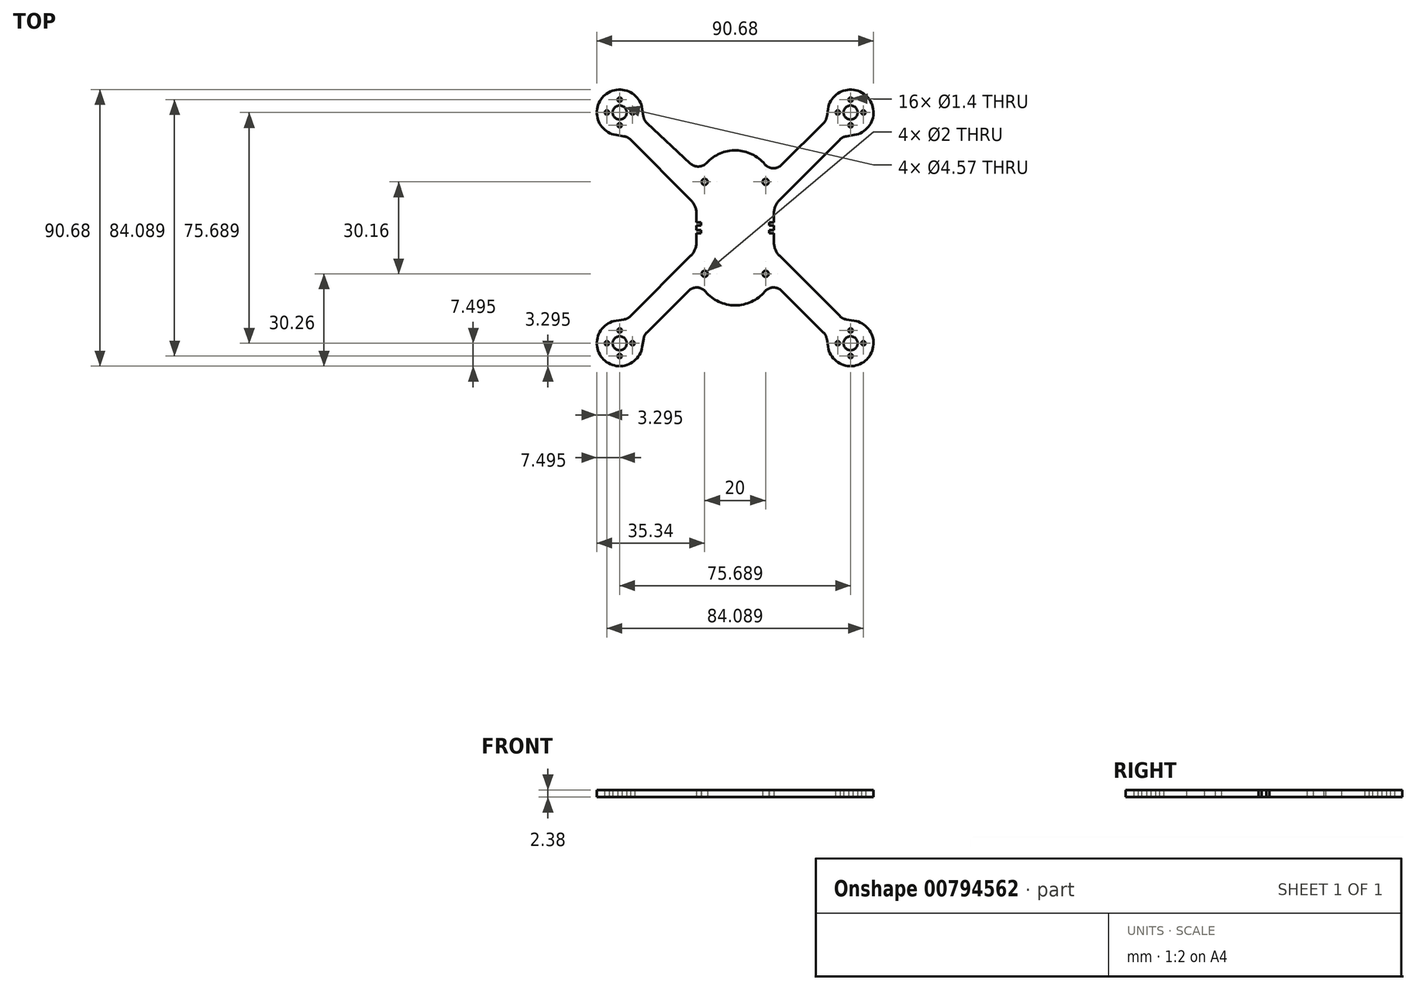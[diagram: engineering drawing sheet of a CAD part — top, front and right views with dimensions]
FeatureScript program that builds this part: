
annotation { "Feature Type Name" : "Feature", "Feature Type Description" : "" }
export const myFeature = defineFeature(function(context is Context, id is Id, definition is map)
    precondition{}
    {
        {
            var Q0;
            Q0=qCreatedBy(makeId("Top.planeOp"),FACE);
            var sketch = newSketch(context, id + "F0", { "sketchPlane" : qUnion([Q0])});
            skLineSegment(sketch, "E0.bottom", {"start": v(0, -25.4) * mm, "end": v(0, -25.4) * mm});
            skLineSegment(sketch, "E0.top", {"start": v(0, 25.4) * mm, "end": v(0, 25.4) * mm});
            skLineSegment(sketch, "E0.left", {"start": v(12.7, -4.68) * mm, "end": v(12.7, 4.68) * mm});
            skLineSegment(sketch, "E0.right", {"start": v(-12.7, -4.68) * mm, "end": v(-12.7, 4.68) * mm});
            skPoint(sketch, "E0.middle", {"position": v(0, 0) * mm});
            skLineSegment(sketch, "E1", {"start": v(12.7, 12.7) * mm, "end": v(37.84, 37.84) * mm});
            skLineSegment(sketch, "E2", {"start": v(-12.7, 12.7) * mm, "end": v(-37.84, 37.84) * mm});
            skLineSegment(sketch, "E3", {"start": v(-12.7, -12.7) * mm, "end": v(-37.84, -37.84) * mm});
            skLineSegment(sketch, "E4", {"start": v(12.7, -12.7) * mm, "end": v(37.84, -37.84) * mm});
            skPoint(sketch, "E5.visualSharp", {"position": v(12.7, -25.4) * mm});
            skArc(sketch, "E5.filletArc", {"start": v(0, -25.4) * mm, "mid": v(5.34, -24.22) * mm, "end": v(9.69, -20.9) * mm});
            skPoint(sketch, "E6.visualSharp", {"position": v(-12.7, -25.4) * mm});
            skArc(sketch, "E6.filletArc", {"start": v(-9.69, -20.9) * mm, "mid": v(-5.34, -24.22) * mm, "end": v(0, -25.4) * mm});
            skPoint(sketch, "E7.visualSharp", {"position": v(-12.7, 25.4) * mm});
            skArc(sketch, "E7.filletArc", {"start": v(0, 25.4) * mm, "mid": v(-5.07, 24.34) * mm, "end": v(-9.3, 21.35) * mm});
            skPoint(sketch, "E8.visualSharp", {"position": v(12.7, 25.4) * mm});
            skArc(sketch, "E8.filletArc", {"start": v(9.69, 20.9) * mm, "mid": v(5.34, 24.22) * mm, "end": v(0, 25.4) * mm});
            skLineSegment(sketch, "E9.bottom", {"start": v(10, -10) * mm, "end": v(-10, -10) * mm});
            skLineSegment(sketch, "E9.top", {"start": v(10, 10) * mm, "end": v(-10, 10) * mm});
            skLineSegment(sketch, "E9.left", {"start": v(10, -10) * mm, "end": v(10, 10) * mm});
            skLineSegment(sketch, "E9.right", {"start": v(-10, -10) * mm, "end": v(-10, 10) * mm});
            skCircle(sketch, "E10", {"center": v(37.84, -37.84) * mm, "radius": 7.5 * mm});
            skCircle(sketch, "E11", {"center": v(-37.84, -37.84) * mm, "radius": 7.5 * mm});
            skCircle(sketch, "E12", {"center": v(-37.84, 37.84) * mm, "radius": 7.5 * mm});
            skCircle(sketch, "E13", {"center": v(37.84, 37.84) * mm, "radius": 7.5 * mm});
            skLineSegment(sketch, "E14", {"start": v(-32.54, -32.54) * mm, "end": v(-35.24, -29.85) * mm});
            skLineSegment(sketch, "E15", {"start": v(-32.54, -32.54) * mm, "end": v(-29.85, -35.24) * mm});
            skLineSegment(sketch, "E16", {"start": v(-36.46, -30.04) * mm, "end": v(-39, -30.43) * mm});
            skLineSegment(sketch, "E17", {"start": v(-30.04, -36.46) * mm, "end": v(-30.43, -39) * mm});
            skLineSegment(sketch, "E18", {"start": v(-32.54, 32.54) * mm, "end": v(-35.24, 29.85) * mm});
            skLineSegment(sketch, "E19", {"start": v(-32.54, 32.54) * mm, "end": v(-29.85, 35.24) * mm});
            skLineSegment(sketch, "E20", {"start": v(-30.05, 36.54) * mm, "end": v(-30.43, 39) * mm});
            skLineSegment(sketch, "E21", {"start": v(-36.46, 30.04) * mm, "end": v(-39, 30.43) * mm});
            skLineSegment(sketch, "E22", {"start": v(32.54, 32.54) * mm, "end": v(35.24, 29.85) * mm});
            skLineSegment(sketch, "E23", {"start": v(32.54, 32.54) * mm, "end": v(29.85, 35.24) * mm});
            skLineSegment(sketch, "E24", {"start": v(36.46, 30.04) * mm, "end": v(39, 30.43) * mm});
            skLineSegment(sketch, "E25", {"start": v(30.04, 36.46) * mm, "end": v(30.43, 39) * mm});
            skLineSegment(sketch, "E26", {"start": v(-34.36, -28.97) * mm, "end": v(-14.56, -9.17) * mm});
            skLineSegment(sketch, "E27", {"start": v(-28.97, -34.36) * mm, "end": v(-15.3, -20.68) * mm});
            skLineSegment(sketch, "E28", {"start": v(-28.88, 34.34) * mm, "end": v(-14.68, 21.15) * mm});
            skLineSegment(sketch, "E29", {"start": v(-34.36, 28.97) * mm, "end": v(-14.56, 9.17) * mm});
            skLineSegment(sketch, "E30", {"start": v(34.36, 28.97) * mm, "end": v(14.56, 9.17) * mm});
            skLineSegment(sketch, "E31", {"start": v(28.97, 34.36) * mm, "end": v(15.3, 20.68) * mm});
            skLineSegment(sketch, "E32", {"start": v(32.54, -32.54) * mm, "end": v(35.24, -29.85) * mm});
            skLineSegment(sketch, "E33", {"start": v(32.54, -32.54) * mm, "end": v(29.85, -35.24) * mm});
            skLineSegment(sketch, "E34", {"start": v(36.46, -30.04) * mm, "end": v(39, -30.43) * mm});
            skLineSegment(sketch, "E35", {"start": v(30.04, -36.46) * mm, "end": v(30.43, -39) * mm});
            skLineSegment(sketch, "E36", {"start": v(28.97, -34.36) * mm, "end": v(15.3, -20.68) * mm});
            skLineSegment(sketch, "E37", {"start": v(34.36, -28.97) * mm, "end": v(14.56, -9.17) * mm});
            skArc(sketch, "E38.filletArc", {"start": v(-12.7, 4.68) * mm, "mid": v(-13.18, 7.11) * mm, "end": v(-14.56, 9.17) * mm});
            skArc(sketch, "E39.filletArc", {"start": v(14.56, 9.17) * mm, "mid": v(13.18, 7.11) * mm, "end": v(12.7, 4.68) * mm});
            skArc(sketch, "E40.filletArc", {"start": v(12.7, -4.68) * mm, "mid": v(13.18, -7.11) * mm, "end": v(14.56, -9.17) * mm});
            skArc(sketch, "E41.filletArc", {"start": v(-14.56, -9.17) * mm, "mid": v(-13.18, -7.11) * mm, "end": v(-12.7, -4.68) * mm});
            skArc(sketch, "E42.filletArc", {"start": v(-14.68, 21.15) * mm, "mid": v(-11.95, 20.14) * mm, "end": v(-9.3, 21.35) * mm});
            skArc(sketch, "E43.filletArc", {"start": v(9.69, 20.9) * mm, "mid": v(12.44, 19.57) * mm, "end": v(15.3, 20.68) * mm});
            skArc(sketch, "E44.filletArc", {"start": v(15.3, -20.68) * mm, "mid": v(12.44, -19.57) * mm, "end": v(9.69, -20.9) * mm});
            skArc(sketch, "E45.filletArc", {"start": v(-9.69, -20.9) * mm, "mid": v(-12.44, -19.57) * mm, "end": v(-15.3, -20.68) * mm});
            skPoint(sketch, "E46.visualSharp", {"position": v(35.24, -29.85) * mm});
            skArc(sketch, "E46.filletArc", {"start": v(34.36, -28.97) * mm, "mid": v(35.33, -29.67) * mm, "end": v(36.46, -30.04) * mm});
            skPoint(sketch, "E47.visualSharp", {"position": v(29.85, -35.24) * mm});
            skArc(sketch, "E47.filletArc", {"start": v(30.04, -36.46) * mm, "mid": v(29.67, -35.33) * mm, "end": v(28.97, -34.36) * mm});
            skPoint(sketch, "E48.visualSharp", {"position": v(-29.85, -35.24) * mm});
            skArc(sketch, "E48.filletArc", {"start": v(-28.97, -34.36) * mm, "mid": v(-29.67, -35.33) * mm, "end": v(-30.04, -36.46) * mm});
            skPoint(sketch, "E49.visualSharp", {"position": v(-35.24, -29.85) * mm});
            skArc(sketch, "E49.filletArc", {"start": v(-36.46, -30.04) * mm, "mid": v(-35.33, -29.67) * mm, "end": v(-34.36, -28.97) * mm});
            skPoint(sketch, "E50.visualSharp", {"position": v(-35.24, 29.85) * mm});
            skArc(sketch, "E50.filletArc", {"start": v(-34.36, 28.97) * mm, "mid": v(-35.33, 29.67) * mm, "end": v(-36.46, 30.04) * mm});
            skPoint(sketch, "E51.visualSharp", {"position": v(-29.85, 35.24) * mm});
            skArc(sketch, "E51.filletArc", {"start": v(-30.05, 36.54) * mm, "mid": v(-29.65, 35.34) * mm, "end": v(-28.88, 34.34) * mm});
            skPoint(sketch, "E52.visualSharp", {"position": v(35.24, 29.85) * mm});
            skArc(sketch, "E52.filletArc", {"start": v(36.46, 30.04) * mm, "mid": v(35.33, 29.67) * mm, "end": v(34.36, 28.97) * mm});
            skPoint(sketch, "E53.visualSharp", {"position": v(29.85, 35.24) * mm});
            skArc(sketch, "E53.filletArc", {"start": v(28.97, 34.36) * mm, "mid": v(29.67, 35.33) * mm, "end": v(30.04, 36.46) * mm});
            skLineSegment(sketch, "E54", {"start": v(12.7, 0) * mm, "end": v(12.7, 0.76) * mm});
            skLineSegment(sketch, "E55", {"start": v(12.7, 0) * mm, "end": v(12.7, -0.76) * mm});
            skLineSegment(sketch, "E56.bottom", {"start": v(12.7, 0.76) * mm, "end": v(11.18, 0.76) * mm});
            skLineSegment(sketch, "E56.top", {"start": v(12.7, 1.78) * mm, "end": v(11.18, 1.78) * mm});
            skLineSegment(sketch, "E56.left", {"start": v(12.7, 0.76) * mm, "end": v(12.7, 1.78) * mm});
            skLineSegment(sketch, "E56.right", {"start": v(11.18, 0.76) * mm, "end": v(11.18, 1.78) * mm});
            skLineSegment(sketch, "E57.bottom", {"start": v(12.7, -0.76) * mm, "end": v(11.18, -0.76) * mm});
            skLineSegment(sketch, "E57.top", {"start": v(12.7, -1.78) * mm, "end": v(11.18, -1.78) * mm});
            skLineSegment(sketch, "E57.left", {"start": v(12.7, -0.76) * mm, "end": v(12.7, -1.78) * mm});
            skLineSegment(sketch, "E57.right", {"start": v(11.18, -0.76) * mm, "end": v(11.18, -1.78) * mm});
            skLineSegment(sketch, "E58", {"start": v(-12.7, 0) * mm, "end": v(-12.7, 0.76) * mm});
            skLineSegment(sketch, "E59", {"start": v(-12.7, 0) * mm, "end": v(-12.7, -0.76) * mm});
            skLineSegment(sketch, "E60.bottom", {"start": v(-12.7, 0.76) * mm, "end": v(-11.18, 0.76) * mm});
            skLineSegment(sketch, "E60.top", {"start": v(-12.7, 1.78) * mm, "end": v(-11.18, 1.78) * mm});
            skLineSegment(sketch, "E60.left", {"start": v(-12.7, 0.76) * mm, "end": v(-12.7, 1.78) * mm});
            skLineSegment(sketch, "E60.right", {"start": v(-11.18, 0.76) * mm, "end": v(-11.18, 1.78) * mm});
            skLineSegment(sketch, "E61.bottom", {"start": v(-12.7, -0.76) * mm, "end": v(-11.18, -0.76) * mm});
            skLineSegment(sketch, "E61.top", {"start": v(-12.7, -1.78) * mm, "end": v(-11.18, -1.78) * mm});
            skLineSegment(sketch, "E61.left", {"start": v(-12.7, -0.76) * mm, "end": v(-12.7, -1.78) * mm});
            skLineSegment(sketch, "E61.right", {"start": v(-11.18, -0.76) * mm, "end": v(-11.18, -1.78) * mm});
            skCircle(sketch, "E62", {"center": v(-37.84, 37.84) * mm, "radius": 4.2 * mm});
            skLineSegment(sketch, "E63", {"start": v(-37.84, 37.84) * mm, "end": v(-33.64, 37.84) * mm});
            skLineSegment(sketch, "E64", {"start": v(-37.84, 37.84) * mm, "end": v(-37.84, 33.64) * mm});
            skLineSegment(sketch, "E65", {"start": v(-37.84, 37.84) * mm, "end": v(-37.84, 42.04) * mm});
            skLineSegment(sketch, "E66", {"start": v(-37.84, 37.84) * mm, "end": v(-42.04, 37.84) * mm});
            skCircle(sketch, "E67", {"center": v(-37.84, 42.04) * mm, "radius": 0.7 * mm});
            skCircle(sketch, "E68", {"center": v(-33.64, 37.84) * mm, "radius": 0.7 * mm});
            skCircle(sketch, "E69", {"center": v(-37.84, 33.64) * mm, "radius": 0.7 * mm});
            skCircle(sketch, "E70", {"center": v(-42.04, 37.84) * mm, "radius": 0.7 * mm});
            skCircle(sketch, "E71", {"center": v(37.84, 37.84) * mm, "radius": 4.2 * mm});
            skLineSegment(sketch, "E72", {"start": v(37.84, 37.84) * mm, "end": v(33.64, 37.84) * mm});
            skLineSegment(sketch, "E73", {"start": v(37.84, 37.84) * mm, "end": v(37.84, 33.64) * mm});
            skLineSegment(sketch, "E74", {"start": v(37.84, 37.84) * mm, "end": v(42.04, 37.84) * mm});
            skLineSegment(sketch, "E75", {"start": v(37.84, 37.84) * mm, "end": v(37.84, 42.04) * mm});
            skCircle(sketch, "E76", {"center": v(33.64, 37.84) * mm, "radius": 0.7 * mm});
            skCircle(sketch, "E77", {"center": v(37.84, 42.04) * mm, "radius": 0.7 * mm});
            skCircle(sketch, "E78", {"center": v(42.04, 37.84) * mm, "radius": 0.7 * mm});
            skCircle(sketch, "E79", {"center": v(37.84, 33.64) * mm, "radius": 0.7 * mm});
            skCircle(sketch, "E80", {"center": v(37.84, -37.84) * mm, "radius": 4.2 * mm});
            skLineSegment(sketch, "E81", {"start": v(37.84, -37.84) * mm, "end": v(37.84, -33.64) * mm});
            skLineSegment(sketch, "E82", {"start": v(37.84, -37.84) * mm, "end": v(33.64, -37.84) * mm});
            skLineSegment(sketch, "E83", {"start": v(37.84, -37.84) * mm, "end": v(42.04, -37.84) * mm});
            skLineSegment(sketch, "E84", {"start": v(37.84, -37.84) * mm, "end": v(37.84, -42.04) * mm});
            skCircle(sketch, "E85", {"center": v(33.64, -37.84) * mm, "radius": 0.7 * mm});
            skCircle(sketch, "E86", {"center": v(37.84, -33.64) * mm, "radius": 0.7 * mm});
            skCircle(sketch, "E87", {"center": v(42.04, -37.84) * mm, "radius": 0.7 * mm});
            skCircle(sketch, "E88", {"center": v(37.84, -42.04) * mm, "radius": 0.7 * mm});
            skCircle(sketch, "E89", {"center": v(-37.84, -37.84) * mm, "radius": 4.2 * mm});
            skLineSegment(sketch, "E90", {"start": v(-37.84, -37.84) * mm, "end": v(-33.64, -37.84) * mm});
            skLineSegment(sketch, "E91", {"start": v(-37.84, -37.84) * mm, "end": v(-37.84, -33.64) * mm});
            skLineSegment(sketch, "E92", {"start": v(-37.84, -37.84) * mm, "end": v(-37.84, -42.04) * mm});
            skLineSegment(sketch, "E93", {"start": v(-37.84, -37.84) * mm, "end": v(-42.04, -37.84) * mm});
            skCircle(sketch, "E94", {"center": v(-42.04, -37.84) * mm, "radius": 0.7 * mm});
            skCircle(sketch, "E95", {"center": v(-37.84, -33.64) * mm, "radius": 0.7 * mm});
            skCircle(sketch, "E96", {"center": v(-33.64, -37.84) * mm, "radius": 0.7 * mm});
            skCircle(sketch, "E97", {"center": v(-37.84, -42.04) * mm, "radius": 0.7 * mm});
            skCircle(sketch, "E98", {"center": v(37.84, 37.84) * mm, "radius": 2.29 * mm});
            skCircle(sketch, "E99", {"center": v(-37.84, 37.84) * mm, "radius": 2.29 * mm});
            skCircle(sketch, "E100", {"center": v(-37.84, -37.84) * mm, "radius": 2.29 * mm});
            skCircle(sketch, "E101", {"center": v(37.84, -37.84) * mm, "radius": 2.29 * mm});
            skLineSegment(sketch, "E102", {"start": v(-10, 10) * mm, "end": v(-10, 15.08) * mm});
            skLineSegment(sketch, "E103", {"start": v(-10, -10) * mm, "end": v(-10, -15.08) * mm});
            skLineSegment(sketch, "E104", {"start": v(10, -10) * mm, "end": v(10, -15.08) * mm});
            skLineSegment(sketch, "E105", {"start": v(10, 10) * mm, "end": v(10, 15.08) * mm});
            skCircle(sketch, "E106", {"center": v(-10, 15.08) * mm, "radius": 1 * mm});
            skCircle(sketch, "E107", {"center": v(10, 15.08) * mm, "radius": 1 * mm});
            skCircle(sketch, "E108", {"center": v(-10, -15.08) * mm, "radius": 1 * mm});
            skCircle(sketch, "E109", {"center": v(10, -15.08) * mm, "radius": 1 * mm});
            skSolve(sketch);
        }
        {
            var Q0;
            {var subQ5=sQuery(id+"F0.wireOp",EDGE,"E85");var subQ6=sQuery(id+"F0.wireOp",EDGE,"E80");var subQ7=makeQuery(id+"F0.imprint","INTERSECT",VERTEX,{"disambiguationData":[OD(1.0)],"derivedFrom":[subQ6,subQ5]});Q0=makeQuery(id+"F0.imprint","IMPRINT",FACE,{"disambiguationData":[TD([[makeQuery(id+"F0.imprint","IMPRINT",EDGE,{"disambiguationData":[TD([[subQ7,-1.0]])],"derivedFrom":subQ6}),1.0]])]});}
            var Q1;
            {var subQ1=sQuery(id+"F0.wireOp",EDGE,"E71");var subQ7=sQuery(id+"F0.wireOp",EDGE,"E77");var subQ8=makeQuery(id+"F0.imprint","INTERSECT",VERTEX,{"disambiguationData":[OD(1.0)],"derivedFrom":[subQ1,subQ7]});Q1=makeQuery(id+"F0.imprint","IMPRINT",FACE,{"disambiguationData":[TD([[makeQuery(id+"F0.imprint","IMPRINT",EDGE,{"disambiguationData":[TD([[subQ8,-1.0]])],"derivedFrom":subQ1}),1.0]])]});}
            var Q2;
            {var subQ1=sQuery(id+"F0.wireOp",EDGE,"E71");var subQ7=sQuery(id+"F0.wireOp",EDGE,"E78");var subQ9=makeQuery(id+"F0.imprint","INTERSECT",VERTEX,{"disambiguationData":[OD(0.0)],"derivedFrom":[subQ1,subQ7]});Q2=makeQuery(id+"F0.imprint","IMPRINT",FACE,{"disambiguationData":[TD([[makeQuery(id+"F0.imprint","IMPRINT",EDGE,{"disambiguationData":[TD([[subQ9,-1.0]])],"derivedFrom":subQ1}),1.0]])]});}
            var Q3;
            {var subQ1=sQuery(id+"F0.wireOp",EDGE,"E1");var subQ3=sQuery(id+"F0.wireOp",EDGE,"E71");var subQ4=makeQuery(id+"F0.imprint","INTERSECT",VERTEX,{"derivedFrom":[subQ1,subQ3]});Q3=makeQuery(id+"F0.imprint","IMPRINT",FACE,{"disambiguationData":[TD([[makeQuery(id+"F0.imprint","IMPRINT",EDGE,{"disambiguationData":[TD([[subQ4,-1.0]])],"derivedFrom":subQ3}),1.0]])]});}
            var Q4;
            {var subQ1=sQuery(id+"F0.wireOp",EDGE,"E89");var subQ7=sQuery(id+"F0.wireOp",EDGE,"E95");var subQ9=makeQuery(id+"F0.imprint","INTERSECT",VERTEX,{"disambiguationData":[OD(1.0)],"derivedFrom":[subQ1,subQ7]});Q4=makeQuery(id+"F0.imprint","IMPRINT",FACE,{"disambiguationData":[TD([[makeQuery(id+"F0.imprint","IMPRINT",EDGE,{"disambiguationData":[TD([[subQ9,-1.0]])],"derivedFrom":subQ1}),1.0]])]});}
            var Q5;
            Q5=makeQuery(id+"F0.imprint","IMPRINT",FACE,{"disambiguationData":[TD([[makeQuery(id+"F0.imprint","IMPRINT",EDGE,{"derivedFrom":sQuery(id+"F0.wireOp",EDGE,"E9.bottom")}),-1.0]])]});
            var Q6;
            {var subQ1=sQuery(id+"F0.wireOp",EDGE,"E80");var subQ7=sQuery(id+"F0.wireOp",EDGE,"E87");var subQ9=makeQuery(id+"F0.imprint","INTERSECT",VERTEX,{"disambiguationData":[OD(0.0)],"derivedFrom":[subQ1,subQ7]});Q6=makeQuery(id+"F0.imprint","IMPRINT",FACE,{"disambiguationData":[TD([[makeQuery(id+"F0.imprint","IMPRINT",EDGE,{"disambiguationData":[TD([[subQ9,-1.0]])],"derivedFrom":subQ1}),1.0]])]});}
            var Q7;
            {var subQ4=sQuery(id+"F0.wireOp",EDGE,"E12");var subQ15=makeQuery(id+"F0.imprint","IMPRINT",VERTEX,{"derivedFrom":subQ4});Q7=makeQuery(id+"F0.imprint","IMPRINT",FACE,{"disambiguationData":[TD([[makeQuery(id+"F0.imprint","IMPRINT",EDGE,{"disambiguationData":[TD([[subQ15,1.0]])],"derivedFrom":subQ4}),1.0]])]});}
            var Q8;
            {var subQ1=sQuery(id+"F0.wireOp",EDGE,"E4");var subQ3=sQuery(id+"F0.wireOp",EDGE,"E80");var subQ4=makeQuery(id+"F0.imprint","INTERSECT",VERTEX,{"derivedFrom":[subQ1,subQ3]});Q8=makeQuery(id+"F0.imprint","IMPRINT",FACE,{"disambiguationData":[TD([[makeQuery(id+"F0.imprint","IMPRINT",EDGE,{"disambiguationData":[TD([[subQ4,-1.0]])],"derivedFrom":subQ3}),1.0]])]});}
            var Q9;
            {var subQ1=sQuery(id+"F0.wireOp",EDGE,"E71");var subQ7=sQuery(id+"F0.wireOp",EDGE,"E79");var subQ9=makeQuery(id+"F0.imprint","INTERSECT",VERTEX,{"disambiguationData":[OD(1.0)],"derivedFrom":[subQ1,subQ7]});Q9=makeQuery(id+"F0.imprint","IMPRINT",FACE,{"disambiguationData":[TD([[makeQuery(id+"F0.imprint","IMPRINT",EDGE,{"disambiguationData":[TD([[subQ9,-1.0]])],"derivedFrom":subQ1}),1.0]])]});}
            var Q10;
            {var subQ1=sQuery(id+"F0.wireOp",EDGE,"E2");var subQ3=sQuery(id+"F0.wireOp",EDGE,"E62");var subQ4=makeQuery(id+"F0.imprint","INTERSECT",VERTEX,{"derivedFrom":[subQ1,subQ3]});Q10=makeQuery(id+"F0.imprint","IMPRINT",FACE,{"disambiguationData":[TD([[makeQuery(id+"F0.imprint","IMPRINT",EDGE,{"disambiguationData":[TD([[subQ4,1.0]])],"derivedFrom":subQ3}),1.0]])]});}
            var Q11;
            {var subQ0=sQuery(id+"F0.wireOp",EDGE,"E67");var subQ1=sQuery(id+"F0.wireOp",EDGE,"E62");var subQ2=makeQuery(id+"F0.imprint","INTERSECT",VERTEX,{"disambiguationData":[OD(1.0)],"derivedFrom":[subQ1,subQ0]});Q11=makeQuery(id+"F0.imprint","IMPRINT",FACE,{"disambiguationData":[TD([[makeQuery(id+"F0.imprint","IMPRINT",EDGE,{"disambiguationData":[TD([[subQ2,-1.0]])],"derivedFrom":subQ1}),1.0]])]});}
            var Q12;
            {var subQ4=sQuery(id+"F0.wireOp",EDGE,"E11");var subQ5=makeQuery(id+"F0.imprint","IMPRINT",VERTEX,{"derivedFrom":subQ4});Q12=makeQuery(id+"F0.imprint","IMPRINT",FACE,{"disambiguationData":[TD([[makeQuery(id+"F0.imprint","IMPRINT",EDGE,{"disambiguationData":[TD([[subQ5,-1.0]])],"derivedFrom":subQ4}),1.0]])]});}
            var Q13;
            {var subQ1=sQuery(id+"F0.wireOp",EDGE,"E4");var subQ3=sQuery(id+"F0.wireOp",EDGE,"E80");var subQ4=makeQuery(id+"F0.imprint","INTERSECT",VERTEX,{"derivedFrom":[subQ1,subQ3]});Q13=makeQuery(id+"F0.imprint","IMPRINT",FACE,{"disambiguationData":[TD([[makeQuery(id+"F0.imprint","IMPRINT",EDGE,{"disambiguationData":[TD([[subQ4,1.0]])],"derivedFrom":subQ3}),1.0]])]});}
            var Q14;
            {var subQ1=sQuery(id+"F0.wireOp",EDGE,"E80");var subQ7=sQuery(id+"F0.wireOp",EDGE,"E88");var subQ9=makeQuery(id+"F0.imprint","INTERSECT",VERTEX,{"disambiguationData":[OD(1.0)],"derivedFrom":[subQ1,subQ7]});Q14=makeQuery(id+"F0.imprint","IMPRINT",FACE,{"disambiguationData":[TD([[makeQuery(id+"F0.imprint","IMPRINT",EDGE,{"disambiguationData":[TD([[subQ9,-1.0]])],"derivedFrom":subQ1}),1.0]])]});}
            var Q15;
            {var subQ3=sQuery(id+"F0.wireOp",EDGE,"E94");var subQ5=sQuery(id+"F0.wireOp",EDGE,"E89");var subQ6=makeQuery(id+"F0.imprint","INTERSECT",VERTEX,{"disambiguationData":[OD(1.0)],"derivedFrom":[subQ5,subQ3]});Q15=makeQuery(id+"F0.imprint","IMPRINT",FACE,{"disambiguationData":[TD([[makeQuery(id+"F0.imprint","IMPRINT",EDGE,{"disambiguationData":[TD([[subQ6,-1.0]])],"derivedFrom":subQ5}),1.0]])]});}
            var Q16;
            {var subQ1=sQuery(id+"F0.wireOp",EDGE,"E1");var subQ3=sQuery(id+"F0.wireOp",EDGE,"E71");var subQ4=makeQuery(id+"F0.imprint","INTERSECT",VERTEX,{"derivedFrom":[subQ1,subQ3]});Q16=makeQuery(id+"F0.imprint","IMPRINT",FACE,{"disambiguationData":[TD([[makeQuery(id+"F0.imprint","IMPRINT",EDGE,{"disambiguationData":[TD([[subQ4,1.0]])],"derivedFrom":subQ3}),1.0]])]});}
            var Q17;
            {var subQ1=sQuery(id+"F0.wireOp",EDGE,"E2");var subQ3=sQuery(id+"F0.wireOp",EDGE,"E62");var subQ4=makeQuery(id+"F0.imprint","INTERSECT",VERTEX,{"derivedFrom":[subQ1,subQ3]});Q17=makeQuery(id+"F0.imprint","IMPRINT",FACE,{"disambiguationData":[TD([[makeQuery(id+"F0.imprint","IMPRINT",EDGE,{"disambiguationData":[TD([[subQ4,-1.0]])],"derivedFrom":subQ3}),1.0]])]});}
            var Q18;
            {var subQ3=sQuery(id+"F0.wireOp",EDGE,"E97");var subQ6=sQuery(id+"F0.wireOp",EDGE,"E89");var subQ9=makeQuery(id+"F0.imprint","INTERSECT",VERTEX,{"disambiguationData":[OD(1.0)],"derivedFrom":[subQ6,subQ3]});Q18=makeQuery(id+"F0.imprint","IMPRINT",FACE,{"disambiguationData":[TD([[makeQuery(id+"F0.imprint","IMPRINT",EDGE,{"disambiguationData":[TD([[subQ9,-1.0]])],"derivedFrom":subQ6}),1.0]])]});}
            var Q19;
            {var subQ1=sQuery(id+"F0.wireOp",EDGE,"E62");var subQ7=sQuery(id+"F0.wireOp",EDGE,"E68");var subQ9=makeQuery(id+"F0.imprint","INTERSECT",VERTEX,{"disambiguationData":[OD(0.0)],"derivedFrom":[subQ1,subQ7]});Q19=makeQuery(id+"F0.imprint","IMPRINT",FACE,{"disambiguationData":[TD([[makeQuery(id+"F0.imprint","IMPRINT",EDGE,{"disambiguationData":[TD([[subQ9,-1.0]])],"derivedFrom":subQ1}),1.0]])]});}
            var Q20;
            {var subQ10=sQuery(id+"F0.wireOp",EDGE,"E13");var subQ11=makeQuery(id+"F0.imprint","IMPRINT",VERTEX,{"derivedFrom":subQ10});Q20=makeQuery(id+"F0.imprint","IMPRINT",FACE,{"disambiguationData":[TD([[makeQuery(id+"F0.imprint","IMPRINT",EDGE,{"disambiguationData":[TD([[subQ11,1.0]])],"derivedFrom":subQ10}),1.0]])]});}
            var Q21;
            {var subQ9=sQuery(id+"F0.wireOp",EDGE,"E10");var subQ10=makeQuery(id+"F0.imprint","IMPRINT",VERTEX,{"derivedFrom":subQ9});Q21=makeQuery(id+"F0.imprint","IMPRINT",FACE,{"disambiguationData":[TD([[makeQuery(id+"F0.imprint","IMPRINT",EDGE,{"disambiguationData":[TD([[subQ10,1.0]])],"derivedFrom":subQ9}),1.0]])]});}
            var Q22;
            {var subQ1=sQuery(id+"F0.wireOp",EDGE,"E3");var subQ3=sQuery(id+"F0.wireOp",EDGE,"E89");var subQ4=makeQuery(id+"F0.imprint","INTERSECT",VERTEX,{"derivedFrom":[subQ1,subQ3]});Q22=makeQuery(id+"F0.imprint","IMPRINT",FACE,{"disambiguationData":[TD([[makeQuery(id+"F0.imprint","IMPRINT",EDGE,{"disambiguationData":[TD([[subQ4,-1.0]])],"derivedFrom":subQ3}),1.0]])]});}
            var Q23;
            {var subQ1=sQuery(id+"F0.wireOp",EDGE,"E3");var subQ3=sQuery(id+"F0.wireOp",EDGE,"E89");var subQ4=makeQuery(id+"F0.imprint","INTERSECT",VERTEX,{"derivedFrom":[subQ1,subQ3]});Q23=makeQuery(id+"F0.imprint","IMPRINT",FACE,{"disambiguationData":[TD([[makeQuery(id+"F0.imprint","IMPRINT",EDGE,{"disambiguationData":[TD([[subQ4,1.0]])],"derivedFrom":subQ3}),1.0]])]});}
            var Q24;
            {var subQ1=sQuery(id+"F0.wireOp",EDGE,"E62");var subQ7=sQuery(id+"F0.wireOp",EDGE,"E70");var subQ9=makeQuery(id+"F0.imprint","INTERSECT",VERTEX,{"disambiguationData":[OD(1.0)],"derivedFrom":[subQ1,subQ7]});Q24=makeQuery(id+"F0.imprint","IMPRINT",FACE,{"disambiguationData":[TD([[makeQuery(id+"F0.imprint","IMPRINT",EDGE,{"disambiguationData":[TD([[subQ9,-1.0]])],"derivedFrom":subQ1}),1.0]])]});}
            var Q25;
            Q25=makeQuery(id+"F0.imprint","IMPRINT",FACE,{"disambiguationData":[TD([[makeQuery(id+"F0.imprint","IMPRINT",EDGE,{"derivedFrom":sQuery(id+"F0.wireOp",EDGE,"E5.filletArc")}),1.0]])]});
            extrude(context, id + "F1", {"entities" : qUnion([Q0, Q1, Q2, Q3, Q4, Q5, Q6, Q7, Q8, Q9, Q10, Q11, Q12, Q13, Q14, Q15, Q16, Q17, Q18, Q19, Q20, Q21, Q22, Q23, Q24, Q25]), "depth" : 2.38 * mm, "offsetDistance" : 25.4 * mm});
        }
    });
